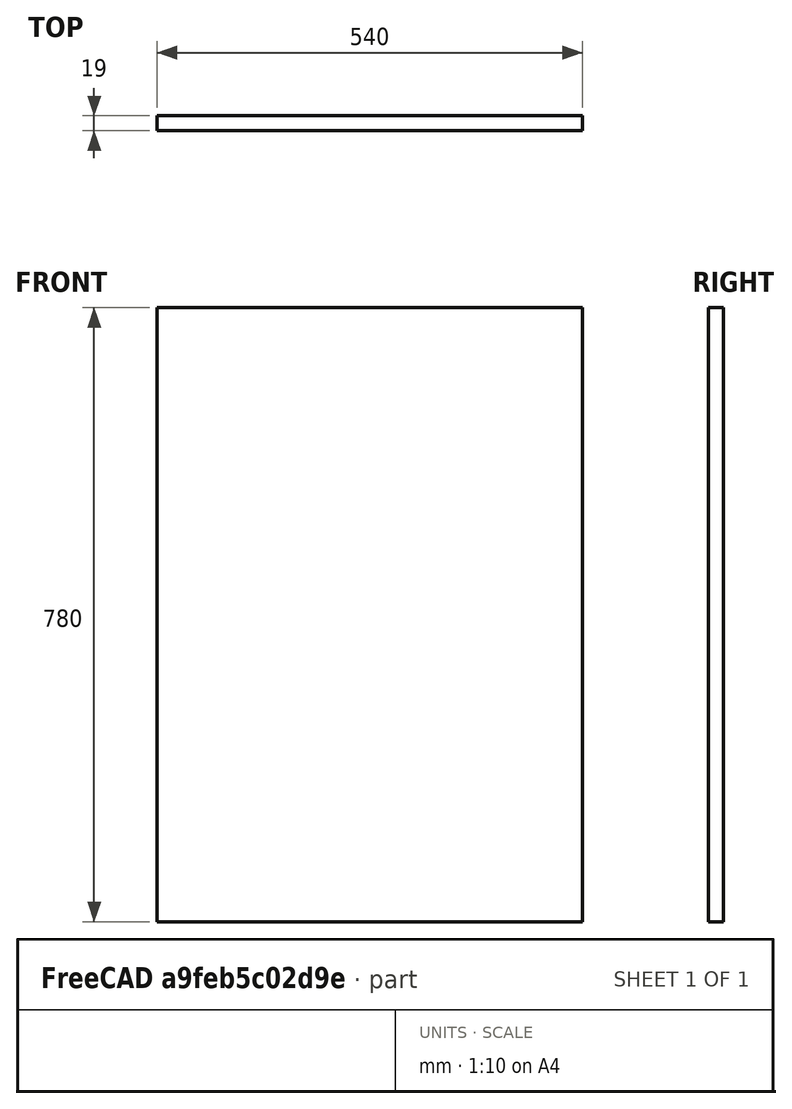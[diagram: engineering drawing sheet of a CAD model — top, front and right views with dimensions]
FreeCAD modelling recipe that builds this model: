
FCSTD DOCUMENT  (FreeCAD 1.0RUnknown)
Label: wardrobe_backplate_corpus02_jan
License: All rights reserved
LicenseURL: https://en.wikipedia.org/wiki/All_rights_reserved
objects: Sketcher::SketchObject×1, PartDesign::Pad×1, PartDesign::CoordinateSystem×1, PartDesign::Body×1
note: 7 computed .brp shape members not serialized (recipe doc carries the construction recipe); baked Part::Feature solids carry a one-line shape summary decoded from their .brp
EXTERNAL_REF file=../../mastersketch.FCStd obj=Spreadsheet

FEATURE [Sketcher::SketchObject] Sketch004
  ArcFitTolerance = 1e-06
  AttachmentSupport = -> [XZ_Plane006]
  FullyConstrained = true
  MakeInternals = false
  MapMode = 5
  Placement = pos=(0,0,0) rot=(1,0,0;1.5708rad)
  expr: Constraints[10] = mastersketch#Spreadsheet.corpus_width
  expr: Constraints[11] = mastersketch#Spreadsheet.corpus02_height
  sketch-geometry (5):
    g0: LineSegment StartX=-270 StartY=-390 StartZ=0 EndX=270 EndY=-390 EndZ=0
    g1: LineSegment StartX=270 StartY=-390 StartZ=0 EndX=270 EndY=390 EndZ=0
    g2: LineSegment StartX=270 StartY=390 StartZ=0 EndX=-270 EndY=390 EndZ=0
    g3: LineSegment StartX=-270 StartY=390 StartZ=0 EndX=-270 EndY=-390 EndZ=0
    g4: GeomPoint [constr] X=0 Y=0 Z=0
  constraints (12):
    c: Coincident(g0,g1)
    c: Coincident(g1,g2)
    c: Coincident(g2,g3)
    c: Coincident(g3,g0)
    c: Horizontal(g0)
    c: Horizontal(g2)
    c: Vertical(g1)
    c: Vertical(g3)
    c: Symmetric(g2,g0,g4)
    c: Coincident(g4,g-1)
    c: DistanceX(g0,g0) = 540
    c: DistanceY(g3,g3) = 780
FEATURE [PartDesign::Pad] Pad004
  Direction = (0,-1,2e-16)
  Length = 19
  Length2 = 10
  Placement = pos=(0,0,0) rot=(1,0,0;1.5708rad)
  Profile = -> Sketch004
  ReferenceAxis = -> Sketch004 [N_Axis]
  Refine = true
  Suppressed = false
  Type = 0
  expr: Length = mastersketch#Spreadsheet.corpus_backplate_thickness
FEATURE [PartDesign::CoordinateSystem] LCS_1
  AttacherType = Attacher::AttachEngine3D
  AttachmentSupport = -> [Pad004]
  MapMode = 45
  Placement = pos=(0,-19,-390) rot=(0.57735,0.57735,0.57735;2.0944rad)
FEATURE [PartDesign::Body] Body004  label="wardrobe_backplate_corpus02_jan"
  AllowCompound = false
  Group = -> [Sketch004,Pad004,LCS_1]
  Origin = -> Origin006
  Tip = -> Pad004
